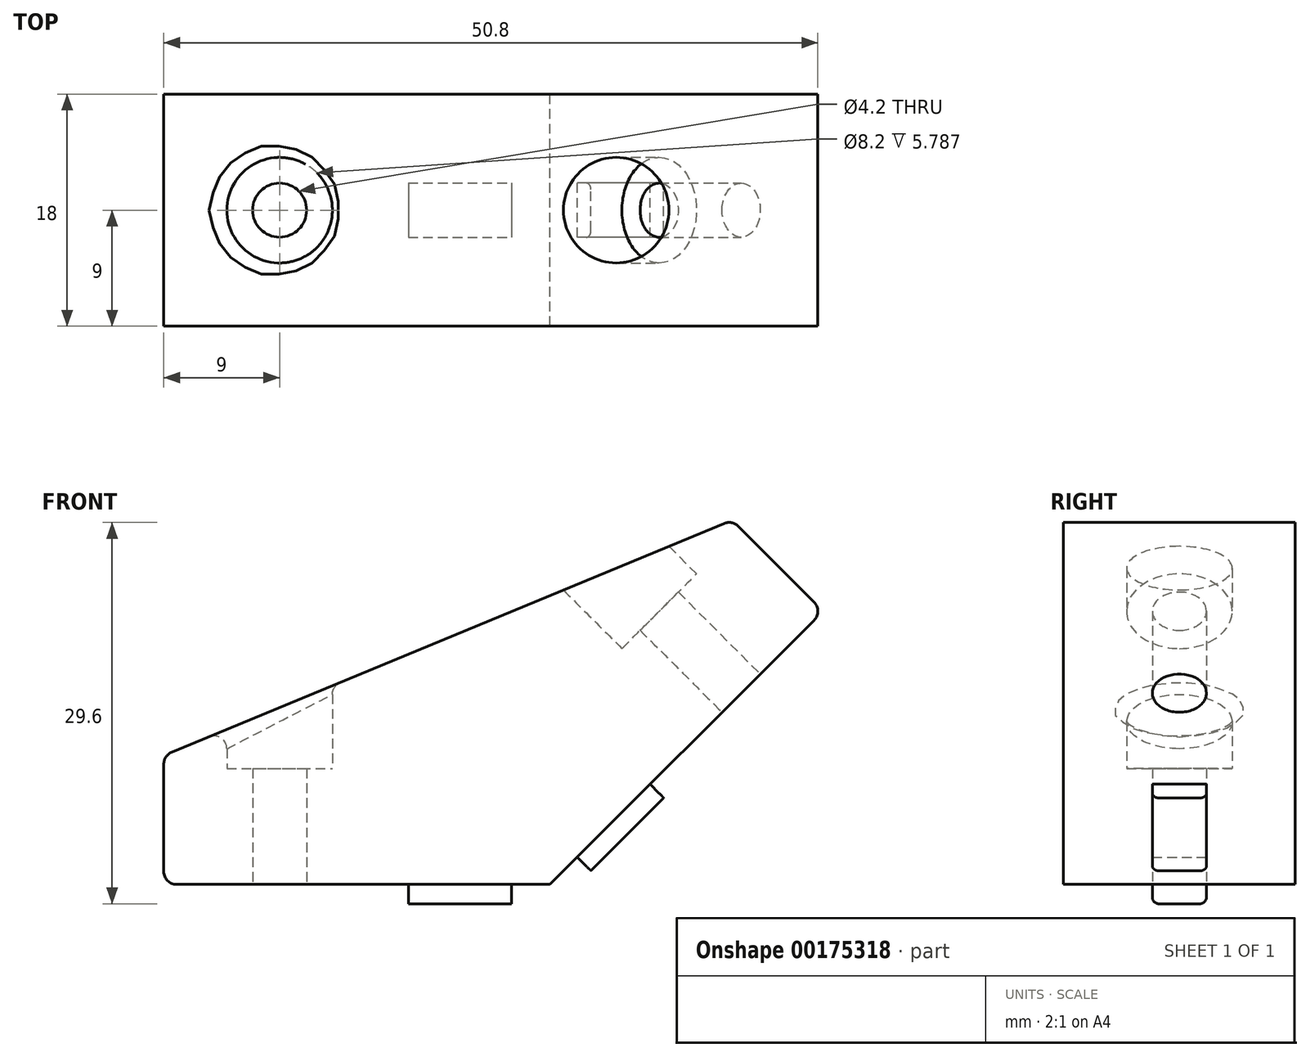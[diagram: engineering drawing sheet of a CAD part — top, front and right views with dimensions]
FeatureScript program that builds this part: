
annotation { "Feature Type Name" : "Feature", "Feature Type Description" : "" }
export const myFeature = defineFeature(function(context is Context, id is Id, definition is map)
    precondition{}
    {
        {
            var Q0;
            Q0=qCreatedBy(makeId("Front.planeOp"),FACE);
            var sketch = newSketch(context, id + "F0", { "sketchPlane" : qUnion([Q0])});
            skLineSegment(sketch, "E0", {"start": v(-30, 0) * mm, "end": v(0, 0) * mm});
            skLineSegment(sketch, "E1", {"start": v(0, 0) * mm, "end": v(21.21, 21.21) * mm});
            skLineSegment(sketch, "E2", {"start": v(21.21, 21.21) * mm, "end": v(14.14, 28.28) * mm});
            skLineSegment(sketch, "E3", {"start": v(14.14, 28.28) * mm, "end": v(-30, 10) * mm});
            skLineSegment(sketch, "E4", {"start": v(-30, 10) * mm, "end": v(-30, 0) * mm});
            skSolve(sketch);
        }
        {
            var Q0;
            Q0=makeQuery(id+"F0.imprint","IMPRINT",FACE,{"disambiguationData":[TD([[makeQuery(id+"F0.imprint","IMPRINT",EDGE,{"derivedFrom":sQuery(id+"F0.wireOp",EDGE,"E0")}),1.0]])]});
            extrude(context, id + "F1", {"entities" : qUnion([Q0]), "depth" : 18 * mm, "offsetDistance" : 25 * mm});
        }
        {
            var Q0;
            Q0=makeQuery(id+"F1.opExtrude","SWEPT_FACE",FACE,{"disambiguationData":[OSD([sQuery(id+"F0.wireOp",EDGE,"E0")])]});
            var sketch = newSketch(context, id + "F2", { "sketchPlane" : qUnion([Q0])});
            skCircle(sketch, "E5", {"center": v(-21, 9) * mm, "radius": 4.1 * mm});
            skPoint(sketch, "E5.centerSnap0", {"position": v(-30, 9) * mm});
            skCircle(sketch, "E6", {"center": v(-21, 9) * mm, "radius": 2.1 * mm});
            skLineSegment(sketch, "E7.bottom", {"start": v(-11, 6.9) * mm, "end": v(-3, 6.9) * mm});
            skLineSegment(sketch, "E7.top", {"start": v(-11, 11.1) * mm, "end": v(-3, 11.1) * mm});
            skLineSegment(sketch, "E7.left", {"start": v(-11, 6.9) * mm, "end": v(-11, 11.1) * mm});
            skLineSegment(sketch, "E7.right", {"start": v(-3, 6.9) * mm, "end": v(-3, 11.1) * mm});
            skPoint(sketch, "E7.middle", {"position": v(-7, 9) * mm});
            skSolve(sketch);
        }
        {
            var Q0;
            Q0=makeQuery(id+"F2.imprint","IMPRINT",FACE,{"disambiguationData":[TD([[makeQuery(id+"F2.imprint","IMPRINT",EDGE,{"derivedFrom":sQuery(id+"F2.wireOp",EDGE,"E6")}),1.0]])]});
            extrude(context, id + "F3", {"entities" : qUnion([Q0]), "operationType" : NewBodyOperationType.REMOVE, "oppositeDirection" : true, "depth" : 25 * mm, "offsetDistance" : 25 * mm});
        }
        {
            var Q0;
            Q0=makeQuery(id+"F2.imprint","IMPRINT",FACE,{"disambiguationData":[TD([[makeQuery(id+"F2.imprint","IMPRINT",EDGE,{"derivedFrom":sQuery(id+"F2.wireOp",EDGE,"E5")}),1.0]])]});
            extrude(context, id + "F4", {"entities" : qUnion([Q0]), "operationType" : NewBodyOperationType.REMOVE, "oppositeDirection" : true, "depth" : 25 * mm, "offsetDistance" : 25 * mm, "hasSecondDirection" : true, "secondDirectionOppositeDirection" : true, "secondDirectionDepth" : 9 * mm});
        }
        {
            var Q0;
            Q0=makeQuery(id+"F1.opExtrude","SWEPT_FACE",FACE,{"disambiguationData":[OSD([sQuery(id+"F0.wireOp",EDGE,"E1")])]});
            var sketch = newSketch(context, id + "F5", { "sketchPlane" : qUnion([Q0])});
            skCircle(sketch, "E8", {"center": v(-9, 21) * mm, "radius": 2.1 * mm});
            skPoint(sketch, "E8.centerSnap0", {"position": v(-9, 30) * mm});
            skCircle(sketch, "E9", {"center": v(-9, 21) * mm, "radius": 4.1 * mm});
            skLineSegment(sketch, "E10.bottom", {"start": v(-11.1, 11) * mm, "end": v(-6.9, 11) * mm});
            skLineSegment(sketch, "E10.top", {"start": v(-11.1, 3) * mm, "end": v(-6.9, 3) * mm});
            skLineSegment(sketch, "E10.left", {"start": v(-11.1, 11) * mm, "end": v(-11.1, 3) * mm});
            skLineSegment(sketch, "E10.right", {"start": v(-6.9, 11) * mm, "end": v(-6.9, 3) * mm});
            skPoint(sketch, "E10.middle", {"position": v(-9, 7) * mm});
            skSolve(sketch);
        }
        {
            var Q0;
            Q0=makeQuery(id+"F5.imprint","IMPRINT",FACE,{"disambiguationData":[TD([[makeQuery(id+"F5.imprint","IMPRINT",EDGE,{"derivedFrom":sQuery(id+"F5.wireOp",EDGE,"E8")}),-1.0]])]});
            extrude(context, id + "F6", {"entities" : qUnion([Q0]), "operationType" : NewBodyOperationType.REMOVE, "oppositeDirection" : true, "depth" : 25 * mm, "offsetDistance" : 25 * mm, "hasSecondDirection" : true, "secondDirectionOppositeDirection" : true, "secondDirectionDepth" : 9 * mm});
        }
        {
            var Q0;
            Q0=makeQuery(id+"F5.imprint","IMPRINT",FACE,{"disambiguationData":[TD([[makeQuery(id+"F5.imprint","IMPRINT",EDGE,{"derivedFrom":sQuery(id+"F5.wireOp",EDGE,"E8")}),1.0]])]});
            extrude(context, id + "F7", {"entities" : qUnion([Q0]), "operationType" : NewBodyOperationType.REMOVE, "oppositeDirection" : true, "depth" : 25 * mm, "offsetDistance" : 25 * mm});
        }
        {
            var Q0;
            Q0=makeQuery(id+"F1.opExtrude","SWEPT_EDGE",EDGE,{"disambiguationData":[OSD([sQuery(id+"F0.wireOp",EDGE,"E0"),sQuery(id+"F0.wireOp",EDGE,"E4")])]});
            var Q1;
            Q1=makeQuery(id+"F1.opExtrude","SWEPT_EDGE",EDGE,{"disambiguationData":[OSD([sQuery(id+"F0.wireOp",EDGE,"E3"),sQuery(id+"F0.wireOp",EDGE,"E4")])]});
            var Q2;
            Q2=makeQuery(id+"F1.opExtrude","SWEPT_EDGE",EDGE,{"disambiguationData":[OSD([sQuery(id+"F0.wireOp",EDGE,"E1"),sQuery(id+"F0.wireOp",EDGE,"E2")])]});
            var Q3;
            Q3=makeQuery(id+"F1.opExtrude","SWEPT_EDGE",EDGE,{"disambiguationData":[OSD([sQuery(id+"F0.wireOp",EDGE,"E2"),sQuery(id+"F0.wireOp",EDGE,"E3")])]});
            var Q4;
            Q4=makeQuery(id+"F4.boolean.opBoolean","INTERSECT",EDGE,{"derivedFrom":[makeQuery(id+"F1.opExtrude","SWEPT_FACE",FACE,{"disambiguationData":[OSD([sQuery(id+"F0.wireOp",EDGE,"E3")])]}),makeQuery(id+"F4.opExtrude","SWEPT_FACE",FACE,{"disambiguationData":[OSD([sQuery(id+"F2.wireOp",EDGE,"E5")])]})]});
            fillet(context, id + "F8", {"entities" : qUnion([Q0, Q1, Q2, Q3, Q4]), "tangentPropagation" : true, "radius" : 1 * mm, "defaultsChanged" : false, "vertexSettings" : [], "allowEdgeOverflow" : false});
        }
        {
            var Q0;
            Q0=makeQuery(id+"F2.imprint","IMPRINT",FACE,{"disambiguationData":[TD([[makeQuery(id+"F2.imprint","IMPRINT",EDGE,{"derivedFrom":sQuery(id+"F2.wireOp",EDGE,"E7.bottom")}),1.0]])]});
            extrude(context, id + "F9", {"entities" : qUnion([Q0]), "operationType" : NewBodyOperationType.ADD, "depth" : 1.5 * mm, "offsetDistance" : 25 * mm});
        }
        {
            var Q0;
            Q0=makeQuery(id+"F5.imprint","IMPRINT",FACE,{"disambiguationData":[TD([[makeQuery(id+"F5.imprint","IMPRINT",EDGE,{"derivedFrom":sQuery(id+"F5.wireOp",EDGE,"E10.bottom")}),-1.0]])]});
            extrude(context, id + "F10", {"entities" : qUnion([Q0]), "operationType" : NewBodyOperationType.ADD, "depth" : 1.5 * mm, "offsetDistance" : 25 * mm});
        }
        {
            var Q0;
            Q0=makeQuery(id+"F9.opExtrude","CAP_EDGE",EDGE,{"disambiguationData":[OSD([sQuery(id+"F2.wireOp",EDGE,"E7.bottom")])],"isStart":true});
            var Q1;
            Q1=makeQuery(id+"F9.opExtrude","CAP_EDGE",EDGE,{"disambiguationData":[OSD([sQuery(id+"F2.wireOp",EDGE,"E7.bottom")])],"isStart":false});
            var Q2;
            Q2=makeQuery(id+"F9.opExtrude","CAP_EDGE",EDGE,{"disambiguationData":[OSD([sQuery(id+"F2.wireOp",EDGE,"E7.top")])],"isStart":false});
            var Q3;
            Q3=makeQuery(id+"F9.opExtrude","CAP_EDGE",EDGE,{"disambiguationData":[OSD([sQuery(id+"F2.wireOp",EDGE,"E7.top")])],"isStart":true});
            var Q4;
            Q4=makeQuery(id+"F10.opExtrude","CAP_EDGE",EDGE,{"disambiguationData":[OSD([sQuery(id+"F5.wireOp",EDGE,"E10.left")])],"isStart":true});
            var Q5;
            Q5=makeQuery(id+"F10.opExtrude","CAP_EDGE",EDGE,{"disambiguationData":[OSD([sQuery(id+"F5.wireOp",EDGE,"E10.left")])],"isStart":false});
            var Q6;
            Q6=makeQuery(id+"F10.opExtrude","CAP_EDGE",EDGE,{"disambiguationData":[OSD([sQuery(id+"F5.wireOp",EDGE,"E10.right")])],"isStart":false});
            var Q7;
            Q7=makeQuery(id+"F10.opExtrude","CAP_EDGE",EDGE,{"disambiguationData":[OSD([sQuery(id+"F5.wireOp",EDGE,"E10.right")])],"isStart":true});
            fillet(context, id + "F11", {"entities" : qUnion([Q0, Q1, Q2, Q3, Q4, Q5, Q6, Q7]), "tangentPropagation" : true, "radius" : 0.5 * mm, "defaultsChanged" : false, "vertexSettings" : [], "allowEdgeOverflow" : false});
        }
    });
